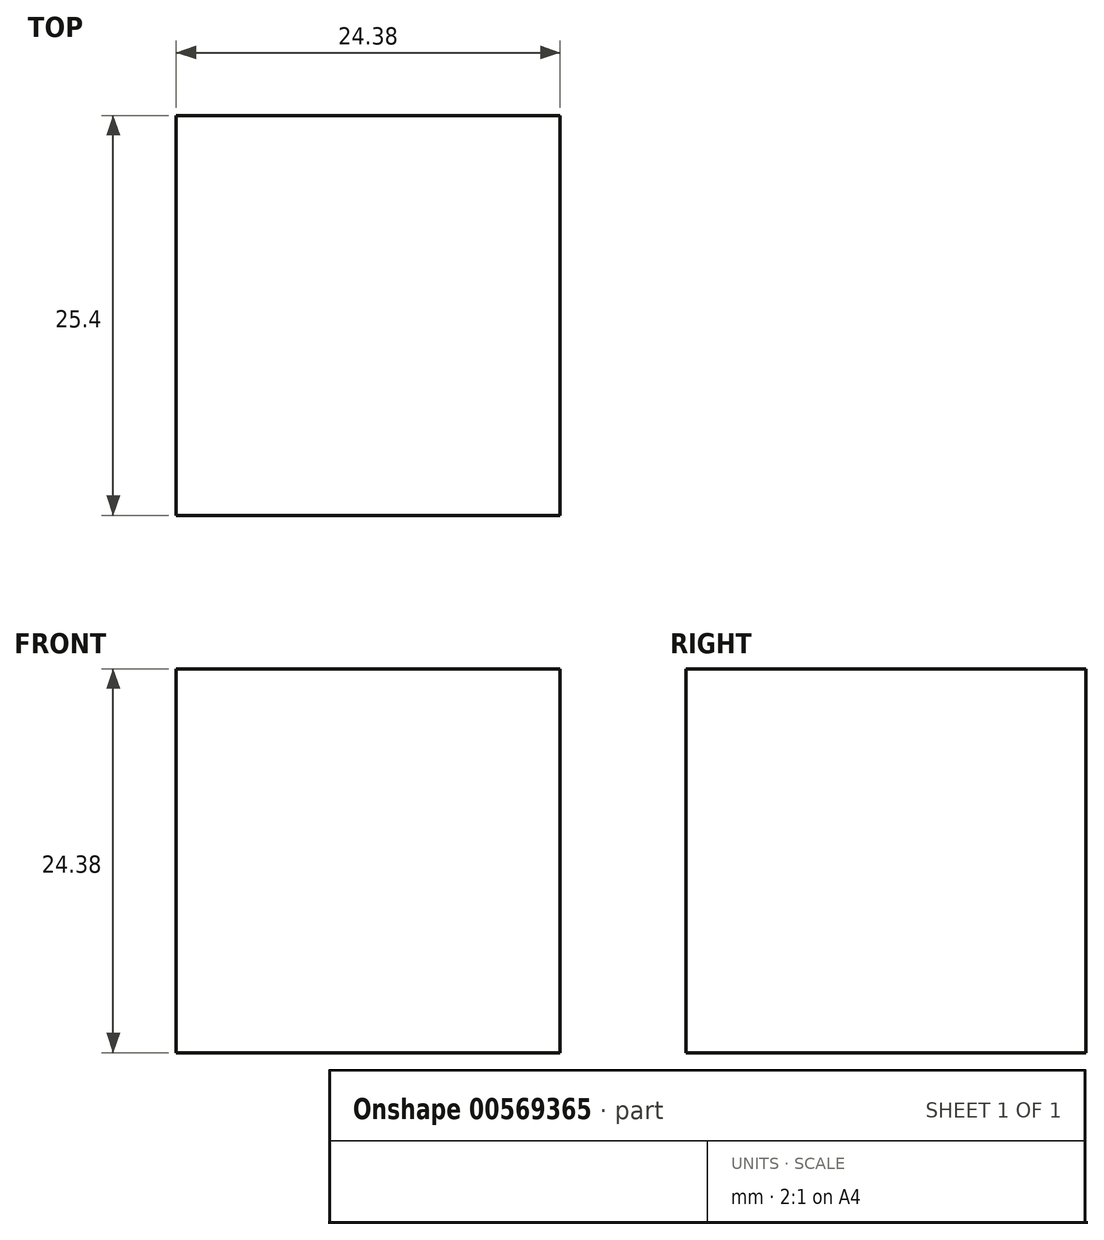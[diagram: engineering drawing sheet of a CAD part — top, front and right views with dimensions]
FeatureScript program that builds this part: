
annotation { "Feature Type Name" : "Feature", "Feature Type Description" : "" }
export const myFeature = defineFeature(function(context is Context, id is Id, definition is map)
    precondition{}
    {
        {
            var Q0;
            Q0=qCreatedBy(makeId("Front.planeOp"),FACE);
            var sketch = newSketch(context, id + "F0", { "sketchPlane" : qUnion([Q0])});
            skLineSegment(sketch, "E0.bottom", {"start": v(12.2, 12.2) * mm, "end": v(-12.2, 12.2) * mm});
            skLineSegment(sketch, "E0.top", {"start": v(12.2, -12.2) * mm, "end": v(-12.2, -12.2) * mm});
            skLineSegment(sketch, "E0.left", {"start": v(12.2, 12.2) * mm, "end": v(12.2, -12.2) * mm});
            skLineSegment(sketch, "E0.right", {"start": v(-12.2, 12.2) * mm, "end": v(-12.2, -12.2) * mm});
            skPoint(sketch, "E0.middle", {"position": v(0, 0) * mm});
            skSolve(sketch);
        }
        {
            var Q0;
            Q0 = qSketchRegion(id + "F0", true);
            extrude(context, id + "F1", {"entities" : qUnion([Q0]), "endBound" : BoundingType.SYMMETRIC, "depth" : 25.4 * mm, "offsetDistance" : 25.4 * mm});
        }
    });
